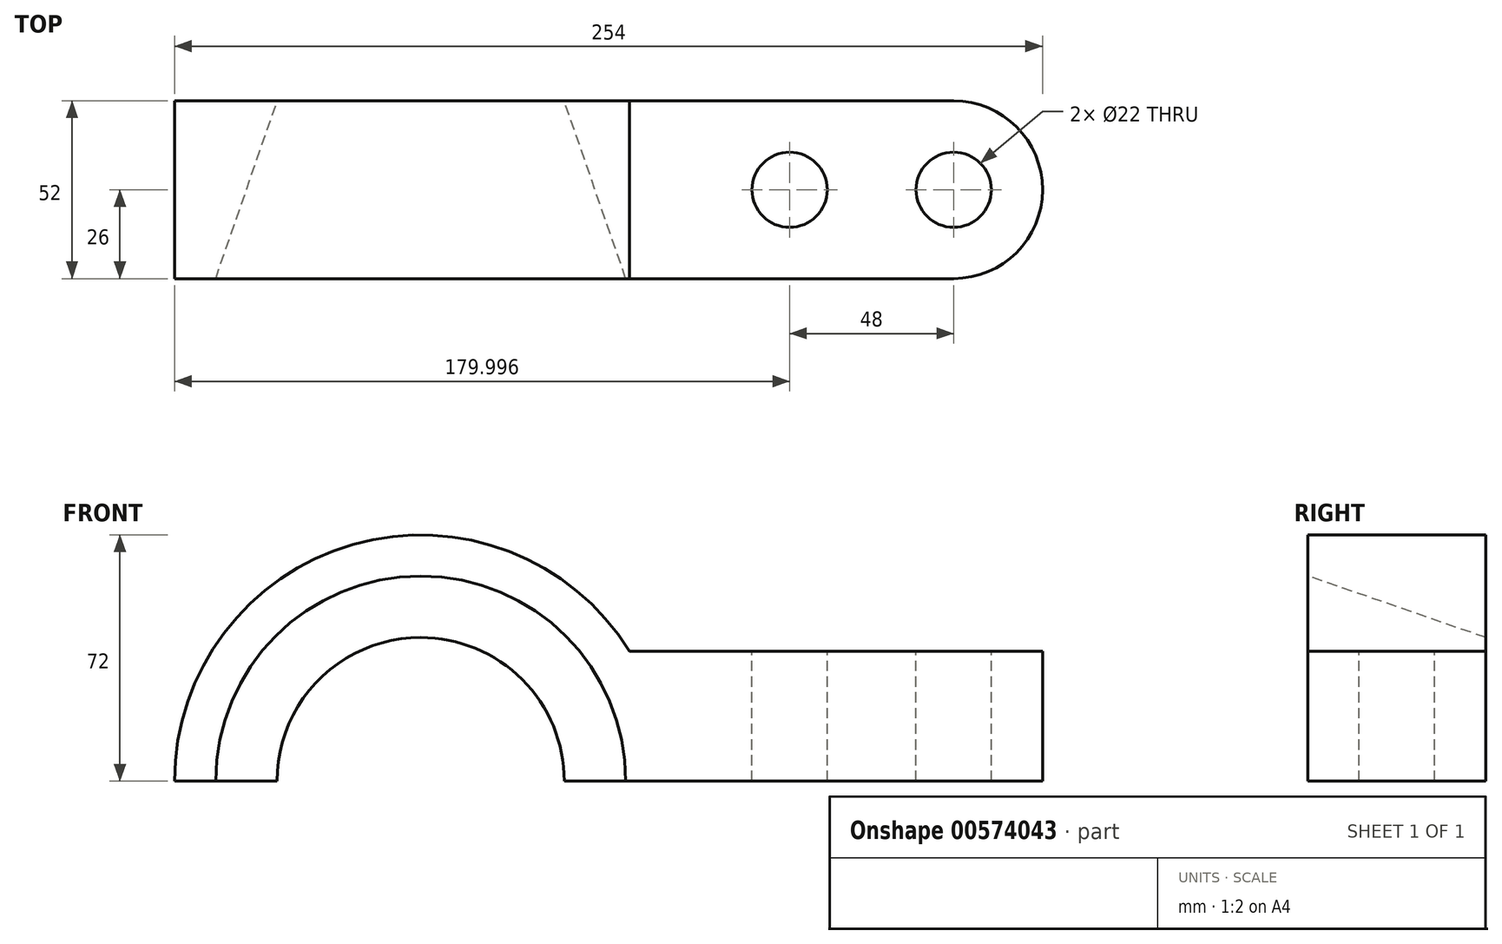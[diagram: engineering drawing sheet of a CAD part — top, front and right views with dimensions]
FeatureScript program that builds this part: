
annotation { "Feature Type Name" : "Feature", "Feature Type Description" : "" }
export const myFeature = defineFeature(function(context is Context, id is Id, definition is map)
    precondition{}
    {
        {
            var Q0;
            Q0=qCreatedBy(makeId("Front.planeOp"),FACE);
            var sketch = newSketch(context, id + "F0", { "sketchPlane" : qUnion([Q0])});
            skLineSegment(sketch, "E0.bottom", {"start": v(46.29, 0) * mm, "end": v(46.29, 0) * mm});
            skLineSegment(sketch, "E0.right", {"start": v(156.29, 0) * mm, "end": v(156.29, 38) * mm});
            skArc(sketch, "E1", {"start": v(16.29, 0) * mm, "mid": v(-25.71, 42) * mm, "end": v(-67.71, 0) * mm});
            skArc(sketch, "E2", {"start": v(35.44, 38) * mm, "mid": v(-45.47, 69.24) * mm, "end": v(-97.71, 0) * mm});
            skLineSegment(sketch, "E3.trimOffspring", {"start": v(35.44, 38) * mm, "end": v(156.29, 38) * mm});
            skLineSegment(sketch, "E4", {"start": v(46.29, 0) * mm, "end": v(156.29, 0) * mm});
            skLineSegment(sketch, "E5", {"start": v(175.97, 0) * mm, "end": v(-103.74, 0) * mm, "construction": true});
            skLineSegment(sketch, "E6", {"start": v(46.29, 0) * mm, "end": v(16.29, 0) * mm});
            skLineSegment(sketch, "E7", {"start": v(-67.71, 0) * mm, "end": v(-97.71, 0) * mm});
            skSolve(sketch);
        }
        {
            var Q0;
            Q0 = qSketchRegion(id + "F0", true);
            extrude(context, id + "F1", {"entities" : qUnion([Q0]), "depth" : 52 * mm, "offsetDistance" : 25 * mm});
        }
        {
            var Q0;
            Q0=makeQuery(id+"F1.opExtrude","SWEPT_FACE",FACE,{"disambiguationData":[OSD([sQuery(id+"F0.wireOp",EDGE,"E3.trimOffspring")])]});
            var sketch = newSketch(context, id + "F2", { "sketchPlane" : qUnion([Q0])});
            skCircle(sketch, "E8", {"center": v(82.29, -26) * mm, "radius": 11 * mm});
            skCircle(sketch, "E9", {"center": v(130.29, -26) * mm, "radius": 11 * mm});
            skSolve(sketch);
        }
        {
            var Q0;
            Q0=makeQuery(id+"F1.opExtrude","CAP_EDGE",EDGE,{"disambiguationData":[OSD([sQuery(id+"F0.wireOp",EDGE,"E0.right")])],"isStart":true});
            var Q1;
            Q1=makeQuery(id+"F1.opExtrude","CAP_EDGE",EDGE,{"disambiguationData":[OSD([sQuery(id+"F0.wireOp",EDGE,"E0.right")])],"isStart":false});
            fillet(context, id + "F3", {"entities" : qUnion([Q0, Q1]), "radius" : 26 * mm, "tangentPropagation" : true, "allowEdgeOverflow" : false});
        }
        {
            var Q0;
            Q0=makeQuery(id+"F2.imprint","IMPRINT",FACE,{"disambiguationData":[TD([[makeQuery(id+"F2.imprint","IMPRINT",EDGE,{"derivedFrom":sQuery(id+"F2.wireOp",EDGE,"E9")}),1.0]])]});
            extrude(context, id + "F4", {"entities" : qUnion([Q0]), "operationType" : NewBodyOperationType.REMOVE, "oppositeDirection" : true, "depth" : 38 * mm, "offsetDistance" : 25 * mm});
        }
        {
            var Q0;
            Q0=makeQuery(id+"F2.imprint","IMPRINT",FACE,{"disambiguationData":[TD([[makeQuery(id+"F2.imprint","IMPRINT",EDGE,{"derivedFrom":sQuery(id+"F2.wireOp",EDGE,"E8")}),1.0]])]});
            extrude(context, id + "F5", {"entities" : qUnion([Q0]), "operationType" : NewBodyOperationType.REMOVE, "oppositeDirection" : true, "depth" : 38 * mm, "offsetDistance" : 25 * mm});
        }
        {
            var Q0;
            Q0=makeQuery(id+"F1.opExtrude","SWEPT_FACE",FACE,{"disambiguationData":[OSD([sQuery(id+"F0.wireOp",EDGE,"E7")])]});
            var sketch = newSketch(context, id + "F6", { "sketchPlane" : qUnion([Q0])});
            skLineSegment(sketch, "E10", {"start": v(-85.66, 52) * mm, "end": v(-67.66, 0) * mm});
            skLineSegment(sketch, "E11", {"start": v(-67.66, 0) * mm, "end": v(-25.66, 0) * mm});
            skLineSegment(sketch, "E12", {"start": v(-25.66, 0) * mm, "end": v(-25.66, 52) * mm});
            skLineSegment(sketch, "E13", {"start": v(-25.66, 52) * mm, "end": v(-85.66, 52) * mm});
            skSolve(sketch);
        }
        {
            var Q0;
            Q0 = qSketchRegion(id + "F6", true);
            var Q1;
            Q1=sQuery(id+"F6.wireOp",EDGE,"E12");
            revolve(context, id + "F7", {"operationType" : NewBodyOperationType.REMOVE, "entities" : qUnion([Q0]), "axis" : qUnion([Q1]), "revolveType" : RevolveType.FULL, "oppositeDirection" : true});
        }
    });
